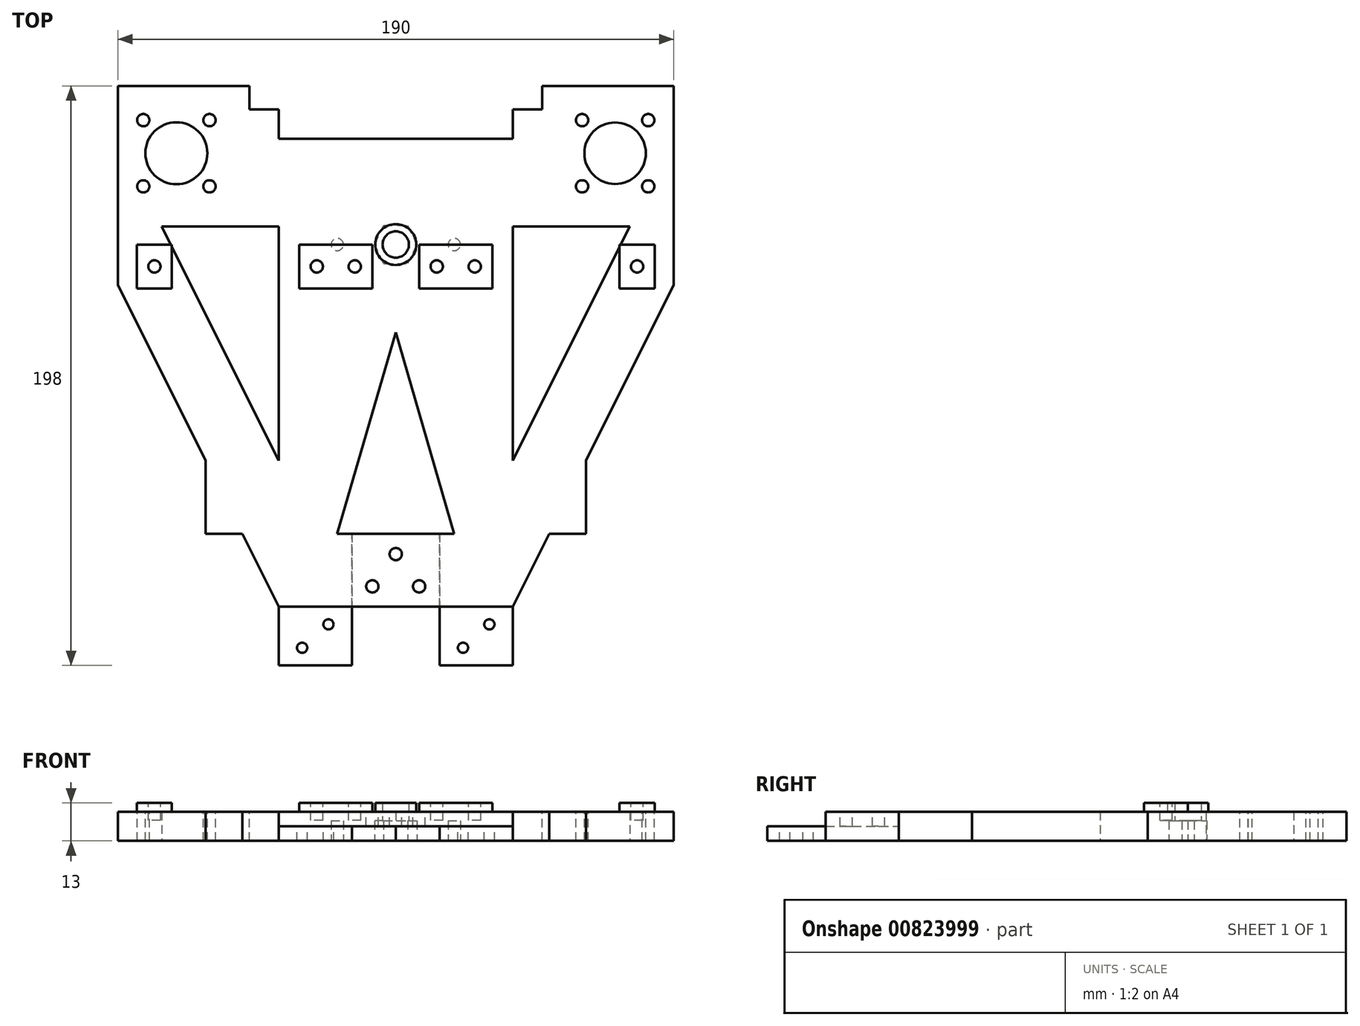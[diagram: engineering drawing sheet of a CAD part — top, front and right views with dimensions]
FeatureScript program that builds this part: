
annotation { "Feature Type Name" : "Feature", "Feature Type Description" : "" }
export const myFeature = defineFeature(function(context is Context, id is Id, definition is map)
    precondition{}
    {
        {
            var Q0;
            Q0=qCreatedBy(makeId("Top.planeOp"),FACE);
            var sketch = newSketch(context, id + "F0", { "sketchPlane" : qUnion([Q0])});
            skCircle(sketch, "E0", {"center": v(-75, 31.2) * mm, "radius": 7 * mm});
            skCircle(sketch, "E1", {"center": v(75, 31.2) * mm, "radius": 7 * mm});
            skCircle(sketch, "E2", {"center": v(0, 0) * mm, "radius": 4.5 * mm});
            skLineSegment(sketch, "E3", {"start": v(-40, -123.8) * mm, "end": v(40, -123.8) * mm});
            skLineSegment(sketch, "E4", {"start": v(40, -123.8) * mm, "end": v(52.5, -98.8) * mm});
            skLineSegment(sketch, "E5", {"start": v(115, 26.2) * mm, "end": v(115, 46.2) * mm});
            skLineSegment(sketch, "E6", {"start": v(115, 46.2) * mm, "end": v(40, 46.2) * mm});
            skLineSegment(sketch, "E7", {"start": v(40, 46.2) * mm, "end": v(40, 36.2) * mm});
            skLineSegment(sketch, "E8", {"start": v(40, 36.2) * mm, "end": v(-40, 36.2) * mm});
            skLineSegment(sketch, "E9", {"start": v(-40, 36.2) * mm, "end": v(-40, 46.2) * mm});
            skLineSegment(sketch, "E10", {"start": v(-40, 46.2) * mm, "end": v(-115, 46.2) * mm});
            skLineSegment(sketch, "E11", {"start": v(-115, 46.2) * mm, "end": v(-115, 26.2) * mm});
            skLineSegment(sketch, "E12", {"start": v(-115, 26.2) * mm, "end": v(-65, -73.8) * mm});
            skLineSegment(sketch, "E13", {"start": v(-20, -98.8) * mm, "end": v(20, -98.8) * mm});
            skLineSegment(sketch, "E14", {"start": v(20, -98.8) * mm, "end": v(0, -30) * mm});
            skLineSegment(sketch, "E15", {"start": v(0, -30) * mm, "end": v(-20, -98.8) * mm});
            skLineSegment(sketch, "E16", {"start": v(40, 6.2) * mm, "end": v(80, 6.2) * mm});
            skLineSegment(sketch, "E17", {"start": v(80, 6.2) * mm, "end": v(40, -73.8) * mm});
            skLineSegment(sketch, "E18", {"start": v(40, -73.8) * mm, "end": v(40, 6.2) * mm});
            skLineSegment(sketch, "E19", {"start": v(-40, 6.2) * mm, "end": v(-80, 6.2) * mm});
            skLineSegment(sketch, "E20", {"start": v(-80, 6.2) * mm, "end": v(-40, -73.8) * mm});
            skLineSegment(sketch, "E21", {"start": v(-40, -73.8) * mm, "end": v(-40, 6.2) * mm});
            skLineSegment(sketch, "E22.bottom", {"start": v(-40, -123.8) * mm, "end": v(-15, -123.8) * mm});
            skLineSegment(sketch, "E22.top", {"start": v(-40, -143.8) * mm, "end": v(-15, -143.8) * mm});
            skLineSegment(sketch, "E22.left", {"start": v(-40, -123.8) * mm, "end": v(-40, -143.8) * mm});
            skLineSegment(sketch, "E22.right", {"start": v(-15, -123.8) * mm, "end": v(-15, -143.8) * mm});
            skLineSegment(sketch, "E23.bottom", {"start": v(40, -123.8) * mm, "end": v(15, -123.8) * mm});
            skLineSegment(sketch, "E23.top", {"start": v(40, -143.8) * mm, "end": v(15, -143.8) * mm});
            skLineSegment(sketch, "E23.left", {"start": v(40, -123.8) * mm, "end": v(40, -143.8) * mm});
            skLineSegment(sketch, "E23.right", {"start": v(15, -123.8) * mm, "end": v(15, -143.8) * mm});
            skLineSegment(sketch, "E24", {"start": v(-65, -73.8) * mm, "end": v(-65, -98.8) * mm});
            skLineSegment(sketch, "E25", {"start": v(-65, -98.8) * mm, "end": v(-52.5, -98.8) * mm});
            skLineSegment(sketch, "E26", {"start": v(65, -73.8) * mm, "end": v(65, -98.8) * mm});
            skLineSegment(sketch, "E27", {"start": v(65, -98.8) * mm, "end": v(52.5, -98.8) * mm});
            skLineSegment(sketch, "E28.trimOffspring", {"start": v(-52.5, -98.8) * mm, "end": v(-40, -123.8) * mm});
            skLineSegment(sketch, "E29.trimOffspring", {"start": v(65, -73.8) * mm, "end": v(115, 26.2) * mm});
            skSolve(sketch);
        }
        {
            var Q0;
            Q0 = qSketchRegion(id + "F0", true);
            extrude(context, id + "F1", {"entities" : qUnion([Q0]), "depth" : 10 * mm, "offsetDistance" : 25 * mm});
        }
        {
            var Q0;
            Q0=makeQuery(id+"F1.opExtrude","CAP_FACE",FACE,{"disambiguationData":[OSD([sQuery(id+"F0.wireOp",EDGE,"E0"),sQuery(id+"F0.wireOp",EDGE,"E1"),sQuery(id+"F0.wireOp",EDGE,"E2"),sQuery(id+"F0.wireOp",EDGE,"E3"),sQuery(id+"F0.wireOp",EDGE,"E4"),sQuery(id+"F0.wireOp",EDGE,"E5"),sQuery(id+"F0.wireOp",EDGE,"E6"),sQuery(id+"F0.wireOp",EDGE,"E7"),sQuery(id+"F0.wireOp",EDGE,"E8"),sQuery(id+"F0.wireOp",EDGE,"E9"),sQuery(id+"F0.wireOp",EDGE,"E10"),sQuery(id+"F0.wireOp",EDGE,"E11"),sQuery(id+"F0.wireOp",EDGE,"E12"),sQuery(id+"F0.wireOp",EDGE,"E13"),sQuery(id+"F0.wireOp",EDGE,"E14"),sQuery(id+"F0.wireOp",EDGE,"E15"),sQuery(id+"F0.wireOp",EDGE,"E16"),sQuery(id+"F0.wireOp",EDGE,"E17"),sQuery(id+"F0.wireOp",EDGE,"E18"),sQuery(id+"F0.wireOp",EDGE,"E19"),sQuery(id+"F0.wireOp",EDGE,"E20"),sQuery(id+"F0.wireOp",EDGE,"E21")])],"isStart":false});
            var sketch = newSketch(context, id + "F2", { "sketchPlane" : qUnion([Q0])});
            skLineSegment(sketch, "E30.bottom", {"start": v(-33, 0) * mm, "end": v(-8, 0) * mm});
            skLineSegment(sketch, "E30.top", {"start": v(-33, -15) * mm, "end": v(-8, -15) * mm});
            skLineSegment(sketch, "E30.left", {"start": v(-33, 0) * mm, "end": v(-33, -15) * mm});
            skLineSegment(sketch, "E30.right", {"start": v(-8, 0) * mm, "end": v(-8, -15) * mm});
            skLineSegment(sketch, "E31.bottom", {"start": v(8, 0) * mm, "end": v(33, 0) * mm});
            skLineSegment(sketch, "E31.top", {"start": v(8, -15) * mm, "end": v(33, -15) * mm});
            skLineSegment(sketch, "E31.left", {"start": v(8, 0) * mm, "end": v(8, -15) * mm});
            skLineSegment(sketch, "E31.right", {"start": v(33, 0) * mm, "end": v(33, -15) * mm});
            skLineSegment(sketch, "E32.bottom", {"start": v(76.5, 0) * mm, "end": v(88.5, 0) * mm});
            skLineSegment(sketch, "E32.top", {"start": v(76.5, -15) * mm, "end": v(88.5, -15) * mm});
            skLineSegment(sketch, "E32.left", {"start": v(76.5, 0) * mm, "end": v(76.5, -15) * mm});
            skLineSegment(sketch, "E32.right", {"start": v(88.5, 0) * mm, "end": v(88.5, -15) * mm});
            skLineSegment(sketch, "E33.bottom", {"start": v(-76.5, 0) * mm, "end": v(-88.5, 0) * mm});
            skLineSegment(sketch, "E33.top", {"start": v(-76.5, -15) * mm, "end": v(-88.5, -15) * mm});
            skLineSegment(sketch, "E33.left", {"start": v(-76.5, 0) * mm, "end": v(-76.5, -15) * mm});
            skLineSegment(sketch, "E33.right", {"start": v(-88.5, 0) * mm, "end": v(-88.5, -15) * mm});
            skCircle(sketch, "E34", {"center": v(0, 0) * mm, "radius": 4.5 * mm});
            skCircle(sketch, "E35", {"center": v(0, 0) * mm, "radius": 7 * mm});
            skSolve(sketch);
        }
        {
            var Q0;
            Q0 = qSketchRegion(id + "F2", true);
            extrude(context, id + "F3", {"entities" : qUnion([Q0]), "operationType" : NewBodyOperationType.ADD, "depth" : 3 * mm, "offsetDistance" : 25 * mm});
        }
        {
            var Q0;
            Q0=makeQuery(id+"F1.opExtrude","CAP_FACE",FACE,{"disambiguationData":[OSD([sQuery(id+"F0.wireOp",EDGE,"E0"),sQuery(id+"F0.wireOp",EDGE,"E1"),sQuery(id+"F0.wireOp",EDGE,"E2"),sQuery(id+"F0.wireOp",EDGE,"E3"),sQuery(id+"F0.wireOp",EDGE,"E4"),sQuery(id+"F0.wireOp",EDGE,"E5"),sQuery(id+"F0.wireOp",EDGE,"E6"),sQuery(id+"F0.wireOp",EDGE,"E7"),sQuery(id+"F0.wireOp",EDGE,"E8"),sQuery(id+"F0.wireOp",EDGE,"E9"),sQuery(id+"F0.wireOp",EDGE,"E10"),sQuery(id+"F0.wireOp",EDGE,"E11"),sQuery(id+"F0.wireOp",EDGE,"E12"),sQuery(id+"F0.wireOp",EDGE,"E13"),sQuery(id+"F0.wireOp",EDGE,"E14"),sQuery(id+"F0.wireOp",EDGE,"E15"),sQuery(id+"F0.wireOp",EDGE,"E16"),sQuery(id+"F0.wireOp",EDGE,"E17"),sQuery(id+"F0.wireOp",EDGE,"E18"),sQuery(id+"F0.wireOp",EDGE,"E19"),sQuery(id+"F0.wireOp",EDGE,"E20"),sQuery(id+"F0.wireOp",EDGE,"E21")])],"isStart":true});
            var sketch = newSketch(context, id + "F4", { "sketchPlane" : qUnion([Q0])});
            skLineSegment(sketch, "E36.bottom", {"start": v(-15, 123.8) * mm, "end": v(15, 123.8) * mm});
            skLineSegment(sketch, "E36.top", {"start": v(-15, 98.8) * mm, "end": v(15, 98.8) * mm});
            skLineSegment(sketch, "E36.left", {"start": v(-15, 123.8) * mm, "end": v(-15, 98.8) * mm});
            skLineSegment(sketch, "E36.right", {"start": v(15, 123.8) * mm, "end": v(15, 98.8) * mm});
            skSolve(sketch);
        }
        {
            var Q0;
            Q0 = qSketchRegion(id + "F4", true);
            extrude(context, id + "F5", {"entities" : qUnion([Q0]), "operationType" : NewBodyOperationType.REMOVE, "oppositeDirection" : true, "depth" : 5 * mm, "offsetDistance" : 25 * mm});
        }
        {
            var Q0;
            Q0=makeQuery(id+"F1.opExtrude","CAP_FACE",FACE,{"disambiguationData":[OSD([sQuery(id+"F0.wireOp",EDGE,"E0"),sQuery(id+"F0.wireOp",EDGE,"E1"),sQuery(id+"F0.wireOp",EDGE,"E2"),sQuery(id+"F0.wireOp",EDGE,"E3"),sQuery(id+"F0.wireOp",EDGE,"E4"),sQuery(id+"F0.wireOp",EDGE,"E5"),sQuery(id+"F0.wireOp",EDGE,"E6"),sQuery(id+"F0.wireOp",EDGE,"E7"),sQuery(id+"F0.wireOp",EDGE,"E8"),sQuery(id+"F0.wireOp",EDGE,"E9"),sQuery(id+"F0.wireOp",EDGE,"E10"),sQuery(id+"F0.wireOp",EDGE,"E11"),sQuery(id+"F0.wireOp",EDGE,"E12"),sQuery(id+"F0.wireOp",EDGE,"E13"),sQuery(id+"F0.wireOp",EDGE,"E14"),sQuery(id+"F0.wireOp",EDGE,"E15"),sQuery(id+"F0.wireOp",EDGE,"E16"),sQuery(id+"F0.wireOp",EDGE,"E17"),sQuery(id+"F0.wireOp",EDGE,"E18"),sQuery(id+"F0.wireOp",EDGE,"E19"),sQuery(id+"F0.wireOp",EDGE,"E20"),sQuery(id+"F0.wireOp",EDGE,"E21"),sQuery(id+"F0.wireOp",EDGE,"E22.top"),sQuery(id+"F0.wireOp",EDGE,"E22.left"),sQuery(id+"F0.wireOp",EDGE,"E22.right"),sQuery(id+"F0.wireOp",EDGE,"E23.top"),sQuery(id+"F0.wireOp",EDGE,"E23.left"),sQuery(id+"F0.wireOp",EDGE,"E23.right"),sQuery(id+"F0.wireOp",EDGE,"E24"),sQuery(id+"F0.wireOp",EDGE,"E25"),sQuery(id+"F0.wireOp",EDGE,"E26"),sQuery(id+"F0.wireOp",EDGE,"E27"),sQuery(id+"F0.wireOp",EDGE,"E28.trimOffspring"),sQuery(id+"F0.wireOp",EDGE,"E29.trimOffspring")])],"isStart":false});
            var sketch = newSketch(context, id + "F6", { "sketchPlane" : qUnion([Q0])});
            skLineSegment(sketch, "E37.bottom", {"start": v(-40, -143.8) * mm, "end": v(-15, -143.8) * mm});
            skLineSegment(sketch, "E37.top", {"start": v(-40, -123.8) * mm, "end": v(-15, -123.8) * mm});
            skLineSegment(sketch, "E37.left", {"start": v(-40, -143.8) * mm, "end": v(-40, -123.8) * mm});
            skLineSegment(sketch, "E37.right", {"start": v(-15, -143.8) * mm, "end": v(-15, -123.8) * mm});
            skLineSegment(sketch, "E38.bottom", {"start": v(15, -123.8) * mm, "end": v(40, -123.8) * mm});
            skLineSegment(sketch, "E38.top", {"start": v(15, -143.8) * mm, "end": v(40, -143.8) * mm});
            skLineSegment(sketch, "E38.left", {"start": v(15, -123.8) * mm, "end": v(15, -143.8) * mm});
            skLineSegment(sketch, "E38.right", {"start": v(40, -123.8) * mm, "end": v(40, -143.8) * mm});
            skSolve(sketch);
        }
        {
            var Q0;
            Q0 = qSketchRegion(id + "F6", true);
            extrude(context, id + "F7", {"entities" : qUnion([Q0]), "operationType" : NewBodyOperationType.REMOVE, "oppositeDirection" : true, "depth" : 5 * mm, "offsetDistance" : 25 * mm});
        }
        {
            var Q0;
            Q0=makeQuery(id+"F1.opExtrude","CAP_FACE",FACE,{"disambiguationData":[OSD([sQuery(id+"F0.wireOp",EDGE,"E0"),sQuery(id+"F0.wireOp",EDGE,"E1"),sQuery(id+"F0.wireOp",EDGE,"E2"),sQuery(id+"F0.wireOp",EDGE,"E3"),sQuery(id+"F0.wireOp",EDGE,"E4"),sQuery(id+"F0.wireOp",EDGE,"E5"),sQuery(id+"F0.wireOp",EDGE,"E6"),sQuery(id+"F0.wireOp",EDGE,"E7"),sQuery(id+"F0.wireOp",EDGE,"E8"),sQuery(id+"F0.wireOp",EDGE,"E9"),sQuery(id+"F0.wireOp",EDGE,"E10"),sQuery(id+"F0.wireOp",EDGE,"E11"),sQuery(id+"F0.wireOp",EDGE,"E12"),sQuery(id+"F0.wireOp",EDGE,"E13"),sQuery(id+"F0.wireOp",EDGE,"E14"),sQuery(id+"F0.wireOp",EDGE,"E15"),sQuery(id+"F0.wireOp",EDGE,"E16"),sQuery(id+"F0.wireOp",EDGE,"E17"),sQuery(id+"F0.wireOp",EDGE,"E18"),sQuery(id+"F0.wireOp",EDGE,"E19"),sQuery(id+"F0.wireOp",EDGE,"E20"),sQuery(id+"F0.wireOp",EDGE,"E21"),sQuery(id+"F0.wireOp",EDGE,"E22.top"),sQuery(id+"F0.wireOp",EDGE,"E22.left"),sQuery(id+"F0.wireOp",EDGE,"E22.right"),sQuery(id+"F0.wireOp",EDGE,"E23.top"),sQuery(id+"F0.wireOp",EDGE,"E23.left"),sQuery(id+"F0.wireOp",EDGE,"E23.right"),sQuery(id+"F0.wireOp",EDGE,"E24"),sQuery(id+"F0.wireOp",EDGE,"E25"),sQuery(id+"F0.wireOp",EDGE,"E26"),sQuery(id+"F0.wireOp",EDGE,"E27"),sQuery(id+"F0.wireOp",EDGE,"E28.trimOffspring"),sQuery(id+"F0.wireOp",EDGE,"E29.trimOffspring")])],"isStart":false});
            var sketch = newSketch(context, id + "F8", { "sketchPlane" : qUnion([Q0])});
            skCircle(sketch, "E39", {"center": v(-32, -137.8) * mm, "radius": 1.75 * mm});
            skCircle(sketch, "E40", {"center": v(-23, -129.8) * mm, "radius": 1.75 * mm});
            skCircle(sketch, "E41", {"center": v(23, -137.8) * mm, "radius": 1.75 * mm});
            skCircle(sketch, "E42", {"center": v(32, -129.8) * mm, "radius": 1.75 * mm});
            skCircle(sketch, "E43", {"center": v(-8, -116.8) * mm, "radius": 2.1 * mm});
            skCircle(sketch, "E44", {"center": v(8, -116.8) * mm, "radius": 2.1 * mm});
            skCircle(sketch, "E45", {"center": v(0, -105.8) * mm, "radius": 2.1 * mm});
            skSolve(sketch);
        }
        {
            var Q0;
            Q0 = qSketchRegion(id + "F8", true);
            extrude(context, id + "F9", {"entities" : qUnion([Q0]), "operationType" : NewBodyOperationType.REMOVE, "oppositeDirection" : true, "depth" : 25 * mm, "offsetDistance" : 25 * mm});
        }
        {
            var Q0;
            Q0=makeQuery(id+"F3.opExtrude","CAP_FACE",FACE,{"disambiguationData":[OSD([sQuery(id+"F2.wireOp",EDGE,"E33.bottom"),sQuery(id+"F2.wireOp",EDGE,"E33.top"),sQuery(id+"F2.wireOp",EDGE,"E33.left"),sQuery(id+"F2.wireOp",EDGE,"E33.right")])],"isStart":false});
            var sketch = newSketch(context, id + "F10", { "sketchPlane" : qUnion([Q0])});
            skCircle(sketch, "E46", {"center": v(-82.5, -7.5) * mm, "radius": 2.1 * mm});
            skCircle(sketch, "E47", {"center": v(-27, -7.5) * mm, "radius": 2.1 * mm});
            skCircle(sketch, "E48", {"center": v(27, -7.5) * mm, "radius": 2.1 * mm});
            skCircle(sketch, "E49", {"center": v(82.5, -7.5) * mm, "radius": 2.1 * mm});
            skCircle(sketch, "E50", {"center": v(-14, -7.5) * mm, "radius": 2.1 * mm});
            skCircle(sketch, "E51", {"center": v(14, -7.5) * mm, "radius": 2.1 * mm});
            skSolve(sketch);
        }
        {
            var Q0;
            Q0 = qSketchRegion(id + "F10", true);
            extrude(context, id + "F11", {"entities" : qUnion([Q0]), "operationType" : NewBodyOperationType.REMOVE, "oppositeDirection" : true, "depth" : 6 * mm, "offsetDistance" : 25 * mm});
        }
        {
            var Q0;
            Q0=makeQuery(id+"F1.opExtrude","CAP_FACE",FACE,{"disambiguationData":[OSD([sQuery(id+"F0.wireOp",EDGE,"E0"),sQuery(id+"F0.wireOp",EDGE,"E1"),sQuery(id+"F0.wireOp",EDGE,"E2"),sQuery(id+"F0.wireOp",EDGE,"E3"),sQuery(id+"F0.wireOp",EDGE,"E4"),sQuery(id+"F0.wireOp",EDGE,"E5"),sQuery(id+"F0.wireOp",EDGE,"E6"),sQuery(id+"F0.wireOp",EDGE,"E7"),sQuery(id+"F0.wireOp",EDGE,"E8"),sQuery(id+"F0.wireOp",EDGE,"E9"),sQuery(id+"F0.wireOp",EDGE,"E10"),sQuery(id+"F0.wireOp",EDGE,"E11"),sQuery(id+"F0.wireOp",EDGE,"E12"),sQuery(id+"F0.wireOp",EDGE,"E13"),sQuery(id+"F0.wireOp",EDGE,"E14"),sQuery(id+"F0.wireOp",EDGE,"E15"),sQuery(id+"F0.wireOp",EDGE,"E16"),sQuery(id+"F0.wireOp",EDGE,"E17"),sQuery(id+"F0.wireOp",EDGE,"E18"),sQuery(id+"F0.wireOp",EDGE,"E19"),sQuery(id+"F0.wireOp",EDGE,"E20"),sQuery(id+"F0.wireOp",EDGE,"E21"),sQuery(id+"F0.wireOp",EDGE,"E22.top"),sQuery(id+"F0.wireOp",EDGE,"E22.left"),sQuery(id+"F0.wireOp",EDGE,"E22.right"),sQuery(id+"F0.wireOp",EDGE,"E23.top"),sQuery(id+"F0.wireOp",EDGE,"E23.left"),sQuery(id+"F0.wireOp",EDGE,"E23.right"),sQuery(id+"F0.wireOp",EDGE,"E24"),sQuery(id+"F0.wireOp",EDGE,"E25"),sQuery(id+"F0.wireOp",EDGE,"E26"),sQuery(id+"F0.wireOp",EDGE,"E27"),sQuery(id+"F0.wireOp",EDGE,"E28.trimOffspring"),sQuery(id+"F0.wireOp",EDGE,"E29.trimOffspring")])],"isStart":false});
            var sketch = newSketch(context, id + "F12", { "sketchPlane" : qUnion([Q0])});
            skLineSegment(sketch, "E52.bottom", {"start": v(-115, 46.2) * mm, "end": v(-95, 46.2) * mm});
            skLineSegment(sketch, "E52.top", {"start": v(-115, -53.8) * mm, "end": v(-95, -53.8) * mm});
            skLineSegment(sketch, "E52.left", {"start": v(-115, 46.2) * mm, "end": v(-115, -53.8) * mm});
            skLineSegment(sketch, "E52.right", {"start": v(-95, 46.2) * mm, "end": v(-95, -53.8) * mm});
            skLineSegment(sketch, "E53.bottom", {"start": v(115, 46.2) * mm, "end": v(95, 46.2) * mm});
            skLineSegment(sketch, "E53.top", {"start": v(115, -58.78) * mm, "end": v(95, -58.78) * mm});
            skLineSegment(sketch, "E53.left", {"start": v(115, 46.2) * mm, "end": v(115, -58.78) * mm});
            skLineSegment(sketch, "E53.right", {"start": v(95, 46.2) * mm, "end": v(95, -58.78) * mm});
            skSolve(sketch);
        }
        {
            var Q0;
            Q0 = qSketchRegion(id + "F12", true);
            extrude(context, id + "F13", {"entities" : qUnion([Q0]), "operationType" : NewBodyOperationType.REMOVE, "oppositeDirection" : true, "depth" : 25 * mm, "offsetDistance" : 25 * mm});
        }
        {
            var Q0;
            Q0=makeQuery(id+"F1.opExtrude","CAP_FACE",FACE,{"disambiguationData":[OSD([sQuery(id+"F0.wireOp",EDGE,"E0"),sQuery(id+"F0.wireOp",EDGE,"E1"),sQuery(id+"F0.wireOp",EDGE,"E2"),sQuery(id+"F0.wireOp",EDGE,"E3"),sQuery(id+"F0.wireOp",EDGE,"E4"),sQuery(id+"F0.wireOp",EDGE,"E5"),sQuery(id+"F0.wireOp",EDGE,"E6"),sQuery(id+"F0.wireOp",EDGE,"E7"),sQuery(id+"F0.wireOp",EDGE,"E8"),sQuery(id+"F0.wireOp",EDGE,"E9"),sQuery(id+"F0.wireOp",EDGE,"E10"),sQuery(id+"F0.wireOp",EDGE,"E11"),sQuery(id+"F0.wireOp",EDGE,"E12"),sQuery(id+"F0.wireOp",EDGE,"E13"),sQuery(id+"F0.wireOp",EDGE,"E14"),sQuery(id+"F0.wireOp",EDGE,"E15"),sQuery(id+"F0.wireOp",EDGE,"E16"),sQuery(id+"F0.wireOp",EDGE,"E17"),sQuery(id+"F0.wireOp",EDGE,"E18"),sQuery(id+"F0.wireOp",EDGE,"E19"),sQuery(id+"F0.wireOp",EDGE,"E20"),sQuery(id+"F0.wireOp",EDGE,"E21"),sQuery(id+"F0.wireOp",EDGE,"E22.top"),sQuery(id+"F0.wireOp",EDGE,"E22.left"),sQuery(id+"F0.wireOp",EDGE,"E22.right"),sQuery(id+"F0.wireOp",EDGE,"E23.top"),sQuery(id+"F0.wireOp",EDGE,"E23.left"),sQuery(id+"F0.wireOp",EDGE,"E23.right"),sQuery(id+"F0.wireOp",EDGE,"E24"),sQuery(id+"F0.wireOp",EDGE,"E25"),sQuery(id+"F0.wireOp",EDGE,"E26"),sQuery(id+"F0.wireOp",EDGE,"E27"),sQuery(id+"F0.wireOp",EDGE,"E28.trimOffspring"),sQuery(id+"F0.wireOp",EDGE,"E29.trimOffspring")])],"isStart":false});
            var sketch = newSketch(context, id + "F14", { "sketchPlane" : qUnion([Q0])});
            skCircle(sketch, "E54", {"center": v(-75, 31.2) * mm, "radius": 10.6 * mm});
            skCircle(sketch, "E55", {"center": v(-75, 31.2) * mm, "radius": 16 * mm, "construction": true});
            skLineSegment(sketch, "E56", {"start": v(-75, 31.2) * mm, "end": v(-51.09, 55.11) * mm, "construction": true});
            skLineSegment(sketch, "E57", {"start": v(-75, 31.2) * mm, "end": v(-39.91, 31.2) * mm, "construction": true});
            skCircle(sketch, "E58", {"center": v(-63.69, 42.51) * mm, "radius": 2.1 * mm});
            skLineSegment(sketch, "E59", {"start": v(-75, 31.2) * mm, "end": v(-63.69, 19.89) * mm, "construction": true});
            skLineSegment(sketch, "E60", {"start": v(-75, 31.2) * mm, "end": v(-86.31, 19.89) * mm, "construction": true});
            skLineSegment(sketch, "E61", {"start": v(-75, 31.2) * mm, "end": v(-86.31, 42.51) * mm, "construction": true});
            skCircle(sketch, "E62", {"center": v(-86.31, 42.51) * mm, "radius": 2.1 * mm});
            skCircle(sketch, "E63", {"center": v(-86.31, 19.89) * mm, "radius": 2.1 * mm});
            skCircle(sketch, "E64", {"center": v(-63.69, 19.89) * mm, "radius": 2.1 * mm});
            skCircle(sketch, "E65", {"center": v(75, 31.2) * mm, "radius": 16 * mm, "construction": true});
            skLineSegment(sketch, "E66", {"start": v(75, 31.2) * mm, "end": v(91, 31.2) * mm, "construction": true});
            skLineSegment(sketch, "E67", {"start": v(75, 31.2) * mm, "end": v(86.31, 42.51) * mm, "construction": true});
            skLineSegment(sketch, "E68", {"start": v(75, 31.2) * mm, "end": v(63.69, 42.51) * mm, "construction": true});
            skLineSegment(sketch, "E69", {"start": v(75, 31.2) * mm, "end": v(63.69, 19.89) * mm, "construction": true});
            skLineSegment(sketch, "E70", {"start": v(75, 31.2) * mm, "end": v(86.31, 19.89) * mm, "construction": true});
            skCircle(sketch, "E71", {"center": v(63.69, 42.51) * mm, "radius": 2.1 * mm});
            skCircle(sketch, "E72", {"center": v(63.69, 19.89) * mm, "radius": 2.1 * mm});
            skCircle(sketch, "E73", {"center": v(86.31, 42.51) * mm, "radius": 2.1 * mm});
            skCircle(sketch, "E74", {"center": v(86.31, 19.89) * mm, "radius": 2.1 * mm});
            skCircle(sketch, "E75", {"center": v(75, 31.2) * mm, "radius": 10.5 * mm});
            skSolve(sketch);
        }
        {
            var Q0;
            Q0 = qSketchRegion(id + "F14", true);
            extrude(context, id + "F15", {"entities" : qUnion([Q0]), "operationType" : NewBodyOperationType.REMOVE, "oppositeDirection" : true, "depth" : 25 * mm, "offsetDistance" : 25 * mm});
        }
        {
            var Q0;
            Q0=makeQuery(id+"F1.opExtrude","CAP_FACE",FACE,{"disambiguationData":[OSD([sQuery(id+"F0.wireOp",EDGE,"E0"),sQuery(id+"F0.wireOp",EDGE,"E1"),sQuery(id+"F0.wireOp",EDGE,"E2"),sQuery(id+"F0.wireOp",EDGE,"E3"),sQuery(id+"F0.wireOp",EDGE,"E4"),sQuery(id+"F0.wireOp",EDGE,"E5"),sQuery(id+"F0.wireOp",EDGE,"E6"),sQuery(id+"F0.wireOp",EDGE,"E7"),sQuery(id+"F0.wireOp",EDGE,"E8"),sQuery(id+"F0.wireOp",EDGE,"E9"),sQuery(id+"F0.wireOp",EDGE,"E10"),sQuery(id+"F0.wireOp",EDGE,"E11"),sQuery(id+"F0.wireOp",EDGE,"E12"),sQuery(id+"F0.wireOp",EDGE,"E13"),sQuery(id+"F0.wireOp",EDGE,"E14"),sQuery(id+"F0.wireOp",EDGE,"E15"),sQuery(id+"F0.wireOp",EDGE,"E16"),sQuery(id+"F0.wireOp",EDGE,"E17"),sQuery(id+"F0.wireOp",EDGE,"E18"),sQuery(id+"F0.wireOp",EDGE,"E19"),sQuery(id+"F0.wireOp",EDGE,"E20"),sQuery(id+"F0.wireOp",EDGE,"E21"),sQuery(id+"F0.wireOp",EDGE,"E22.top"),sQuery(id+"F0.wireOp",EDGE,"E22.left"),sQuery(id+"F0.wireOp",EDGE,"E22.right"),sQuery(id+"F0.wireOp",EDGE,"E23.top"),sQuery(id+"F0.wireOp",EDGE,"E23.left"),sQuery(id+"F0.wireOp",EDGE,"E23.right"),sQuery(id+"F0.wireOp",EDGE,"E24"),sQuery(id+"F0.wireOp",EDGE,"E25"),sQuery(id+"F0.wireOp",EDGE,"E26"),sQuery(id+"F0.wireOp",EDGE,"E27"),sQuery(id+"F0.wireOp",EDGE,"E28.trimOffspring"),sQuery(id+"F0.wireOp",EDGE,"E29.trimOffspring")])],"isStart":false});
            var sketch = newSketch(context, id + "F16", { "sketchPlane" : qUnion([Q0])});
            skLineSegment(sketch, "E76.bottom", {"start": v(-95, 46.2) * mm, "end": v(-50, 46.2) * mm});
            skLineSegment(sketch, "E76.top", {"start": v(-95, 54.2) * mm, "end": v(-50, 54.2) * mm});
            skLineSegment(sketch, "E76.left", {"start": v(-95, 46.2) * mm, "end": v(-95, 54.2) * mm});
            skLineSegment(sketch, "E76.right", {"start": v(-50, 46.2) * mm, "end": v(-50, 54.2) * mm});
            skLineSegment(sketch, "E77.bottom", {"start": v(95, 46.2) * mm, "end": v(50, 46.2) * mm});
            skLineSegment(sketch, "E77.top", {"start": v(95, 54.2) * mm, "end": v(50, 54.2) * mm});
            skLineSegment(sketch, "E77.left", {"start": v(95, 46.2) * mm, "end": v(95, 54.2) * mm});
            skLineSegment(sketch, "E77.right", {"start": v(50, 46.2) * mm, "end": v(50, 54.2) * mm});
            skSolve(sketch);
        }
        {
            var Q0;
            Q0 = qSketchRegion(id + "F16", true);
            extrude(context, id + "F17", {"entities" : qUnion([Q0]), "operationType" : NewBodyOperationType.ADD, "oppositeDirection" : true, "depth" : 10 * mm, "offsetDistance" : 25 * mm});
        }
        {
            var Q0;
            Q0=makeQuery(id+"F17.boolean.opBoolean","MERGE",FACE,{"derivedFrom":[makeQuery(id+"F1.opExtrude","CAP_FACE",FACE,{"disambiguationData":[OSD([sQuery(id+"F0.wireOp",EDGE,"E0"),sQuery(id+"F0.wireOp",EDGE,"E1"),sQuery(id+"F0.wireOp",EDGE,"E2"),sQuery(id+"F0.wireOp",EDGE,"E3"),sQuery(id+"F0.wireOp",EDGE,"E4"),sQuery(id+"F0.wireOp",EDGE,"E5"),sQuery(id+"F0.wireOp",EDGE,"E6"),sQuery(id+"F0.wireOp",EDGE,"E7"),sQuery(id+"F0.wireOp",EDGE,"E8"),sQuery(id+"F0.wireOp",EDGE,"E9"),sQuery(id+"F0.wireOp",EDGE,"E10"),sQuery(id+"F0.wireOp",EDGE,"E11"),sQuery(id+"F0.wireOp",EDGE,"E12"),sQuery(id+"F0.wireOp",EDGE,"E13"),sQuery(id+"F0.wireOp",EDGE,"E14"),sQuery(id+"F0.wireOp",EDGE,"E15"),sQuery(id+"F0.wireOp",EDGE,"E16"),sQuery(id+"F0.wireOp",EDGE,"E17"),sQuery(id+"F0.wireOp",EDGE,"E18"),sQuery(id+"F0.wireOp",EDGE,"E19"),sQuery(id+"F0.wireOp",EDGE,"E20"),sQuery(id+"F0.wireOp",EDGE,"E21"),sQuery(id+"F0.wireOp",EDGE,"E22.top"),sQuery(id+"F0.wireOp",EDGE,"E22.left"),sQuery(id+"F0.wireOp",EDGE,"E22.right"),sQuery(id+"F0.wireOp",EDGE,"E23.top"),sQuery(id+"F0.wireOp",EDGE,"E23.left"),sQuery(id+"F0.wireOp",EDGE,"E23.right"),sQuery(id+"F0.wireOp",EDGE,"E24"),sQuery(id+"F0.wireOp",EDGE,"E25"),sQuery(id+"F0.wireOp",EDGE,"E26"),sQuery(id+"F0.wireOp",EDGE,"E27"),sQuery(id+"F0.wireOp",EDGE,"E28.trimOffspring"),sQuery(id+"F0.wireOp",EDGE,"E29.trimOffspring")])],"isStart":true}),makeQuery(id+"F17.opExtrude","CAP_FACE",FACE,{"disambiguationData":[OSD([sQuery(id+"F16.wireOp",EDGE,"E76.bottom"),sQuery(id+"F16.wireOp",EDGE,"E76.top"),sQuery(id+"F16.wireOp",EDGE,"E76.left"),sQuery(id+"F16.wireOp",EDGE,"E76.right")])],"isStart":false}),makeQuery(id+"F17.opExtrude","CAP_FACE",FACE,{"disambiguationData":[OSD([sQuery(id+"F16.wireOp",EDGE,"E77.bottom"),sQuery(id+"F16.wireOp",EDGE,"E77.top"),sQuery(id+"F16.wireOp",EDGE,"E77.left"),sQuery(id+"F16.wireOp",EDGE,"E77.right")])],"isStart":false})]});
            var sketch = newSketch(context, id + "F18", { "sketchPlane" : qUnion([Q0])});
            skLineSegment(sketch, "E78", {"start": v(-4.12, 6.5) * mm, "end": v(4.12, 6.5) * mm});
            skLineSegment(sketch, "E79", {"start": v(-4.12, 6.5) * mm, "end": v(-7.2, 0) * mm});
            skLineSegment(sketch, "E80", {"start": v(-7.2, 0) * mm, "end": v(-4.12, -6.5) * mm});
            skLineSegment(sketch, "E81", {"start": v(-4.12, -6.5) * mm, "end": v(4.12, -6.5) * mm});
            skLineSegment(sketch, "E82", {"start": v(4.12, -6.5) * mm, "end": v(7.2, 0) * mm});
            skLineSegment(sketch, "E83", {"start": v(7.2, 0) * mm, "end": v(4.12, 6.5) * mm});
            skCircle(sketch, "E84", {"center": v(-20, 0) * mm, "radius": 2.1 * mm});
            skCircle(sketch, "E85", {"center": v(20, 0) * mm, "radius": 2.1 * mm});
            skSolve(sketch);
        }
        {
            var Q0;
            Q0 = qSketchRegion(id + "F18", true);
            extrude(context, id + "F19", {"entities" : qUnion([Q0]), "operationType" : NewBodyOperationType.REMOVE, "oppositeDirection" : true, "depth" : 6.85 * mm, "offsetDistance" : 25 * mm});
        }
    });
